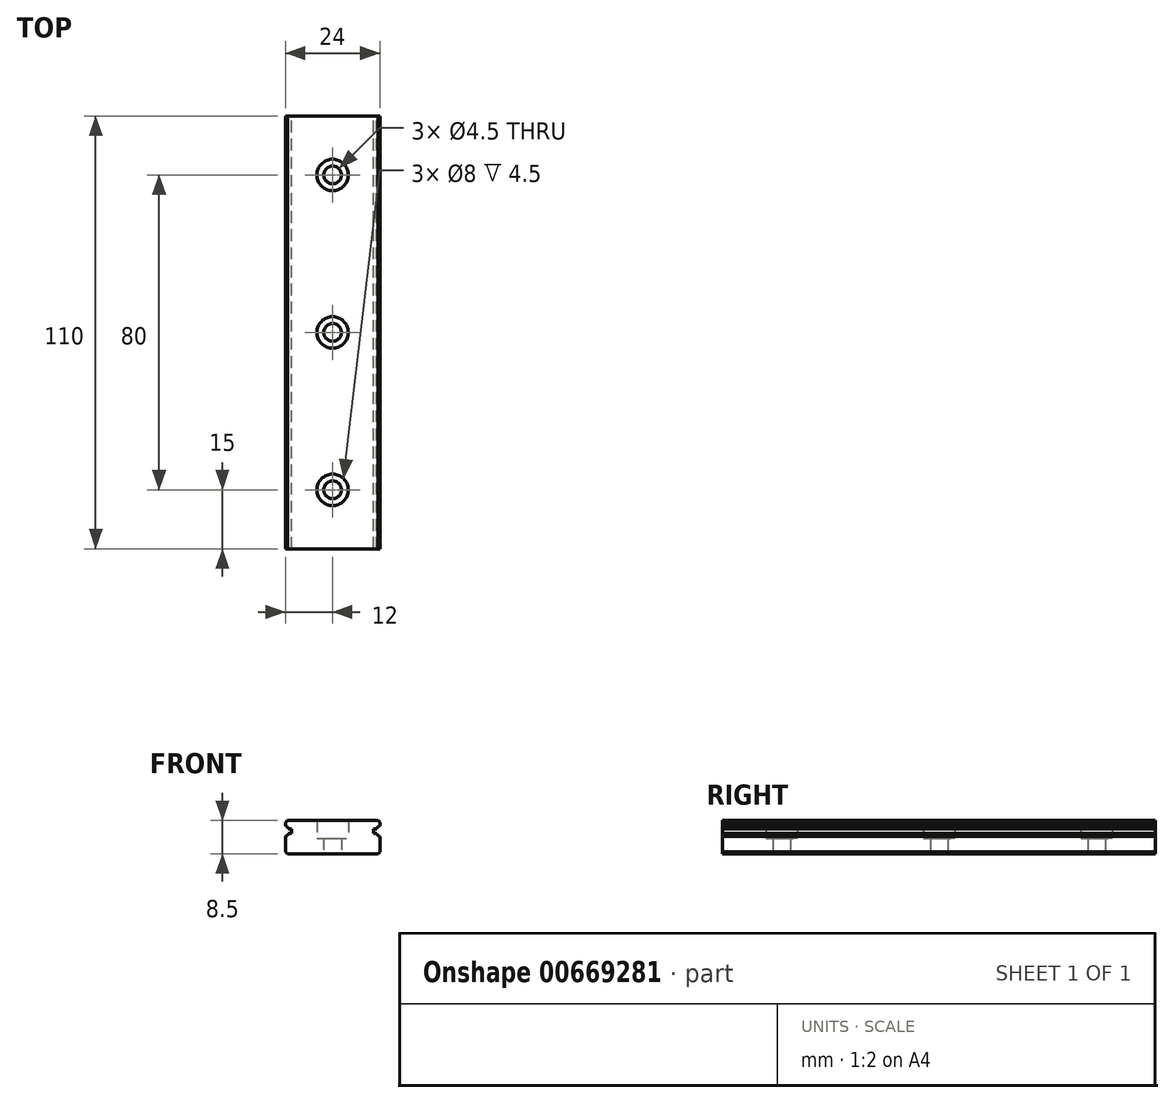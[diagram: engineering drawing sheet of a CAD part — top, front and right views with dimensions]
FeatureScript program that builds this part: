
annotation { "Feature Type Name" : "Feature", "Feature Type Description" : "" }
export const myFeature = defineFeature(function(context is Context, id is Id, definition is map)
    precondition{}
    {
        {
            assignVariable(context, id + "F0", {"variableType" : VariableType.LENGTH, "name" : "D", "lengthValue" : 8 * mm});
        }
        {
            assignVariable(context, id + "F1", {"variableType" : VariableType.LENGTH, "name" : "d", "lengthValue" : 4.5 * mm});
        }
        {
            assignVariable(context, id + "F2", {"variableType" : VariableType.LENGTH, "name" : "h", "lengthValue" : 4.5 * mm});
        }
        {
            var Q0;
            Q0=qCreatedBy(makeId("Front.planeOp"),FACE);
            var sketch = newSketch(context, id + "F3", { "sketchPlane" : qUnion([Q0])});
            skLineSegment(sketch, "E0.bottom", {"start": v(0, -4.25) * mm, "end": v(-11.5, -4.25) * mm});
            skLineSegment(sketch, "E0.right", {"start": v(-12, -3.76) * mm, "end": v(-12, 0.22) * mm});
            skArc(sketch, "E1", {"start": v(-12, 0.22) * mm, "mid": v(-11.5, 0.52) * mm, "end": v(-11.15, 1) * mm});
            skLineSegment(sketch, "E2", {"start": v(-10.45, 1) * mm, "end": v(-11.15, 1) * mm});
            skLineSegment(sketch, "E3", {"start": v(-10.45, 2.1) * mm, "end": v(-11.15, 2.1) * mm});
            skLineSegment(sketch, "E4", {"start": v(-12, 3.76) * mm, "end": v(-11.5, 4.25) * mm});
            skLineSegment(sketch, "E5.MirrorCS", {"start": v(-12, -3.76) * mm, "end": v(-11.5, -4.25) * mm});
            skPoint(sketch, "E6.orphan", {"position": v(-12, 4.25) * mm});
            skLineSegment(sketch, "E7.trimOffspring", {"start": v(-12, 2.88) * mm, "end": v(-12, 3.76) * mm});
            skArc(sketch, "E8.trimOffspring", {"start": v(-11.15, 2.1) * mm, "mid": v(-11.5, 2.58) * mm, "end": v(-12, 2.88) * mm});
            skPoint(sketch, "E9.orphan", {"position": v(-12, -4.25) * mm});
            skLineSegment(sketch, "E10", {"start": v(-11.5, 4.25) * mm, "end": v(0, 4.25) * mm});
            skLineSegment(sketch, "E11", {"start": v(-10.45, 2.1) * mm, "end": v(-10.45, 1) * mm});
            skLineSegment(sketch, "E12", {"start": v(-12.44, 1.55) * mm, "end": v(0, 1.55) * mm, "construction": true});
            skLineSegment(sketch, "E13.MirrorCS", {"start": v(12, 3.76) * mm, "end": v(11.5, 4.25) * mm});
            skLineSegment(sketch, "E14.MirrorCS", {"start": v(12, -3.76) * mm, "end": v(11.5, -4.25) * mm});
            skLineSegment(sketch, "E15.MirrorCS", {"start": v(10.45, 2.1) * mm, "end": v(10.45, 1) * mm});
            skLineSegment(sketch, "E16.MirrorCS", {"start": v(12, 2.88) * mm, "end": v(12, 3.76) * mm});
            skPoint(sketch, "E17.MirrorP", {"position": v(12, 4.25) * mm});
            skPoint(sketch, "E18.MirrorP", {"position": v(12, -4.25) * mm});
            skLineSegment(sketch, "E19.MirrorCS", {"start": v(12, -3.76) * mm, "end": v(12, 0.22) * mm});
            skArc(sketch, "E20.MirrorCS", {"start": v(12, 0.22) * mm, "mid": v(11.5, 0.52) * mm, "end": v(11.15, 1) * mm});
            skLineSegment(sketch, "E21.MirrorCS", {"start": v(10.45, 1) * mm, "end": v(11.15, 1) * mm});
            skLineSegment(sketch, "E22.MirrorCS", {"start": v(10.45, 2.1) * mm, "end": v(11.15, 2.1) * mm});
            skArc(sketch, "E23.MirrorCS", {"start": v(11.15, 2.1) * mm, "mid": v(11.5, 2.58) * mm, "end": v(12, 2.88) * mm});
            skLineSegment(sketch, "E24.MirrorCS", {"start": v(11.5, 4.25) * mm, "end": v(0, 4.25) * mm});
            skLineSegment(sketch, "E25.MirrorCS", {"start": v(0, -4.25) * mm, "end": v(11.5, -4.25) * mm});
            skSolve(sketch);
        }
        {
            var Q0;
            Q0=makeQuery(id+"F3.imprint","IMPRINT",FACE,{"disambiguationData":[TD([[makeQuery(id+"F3.imprint","IMPRINT",EDGE,{"derivedFrom":sQuery(id+"F3.wireOp",EDGE,"E0.bottom")}),-1.0]])]});
            extrude(context, id + "F4", {"entities" : qUnion([Q0]), "depth" : 110 * mm, "offsetDistance" : 25 * mm});
        }
        {
            var Q0;
            Q0=makeQuery(id+"F4.opExtrude","SWEPT_FACE",FACE,{"disambiguationData":[OSD([sQuery(id+"F3.wireOp",EDGE,"E10"),sQuery(id+"F3.wireOp",EDGE,"E24.MirrorCS")])]});
            var sketch = newSketch(context, id + "F5", { "sketchPlane" : qUnion([Q0])});
            skPoint(sketch, "E26", {"position": v(0, -15) * mm});
            skPoint(sketch, "E27.0.1.0", {"position": v(0, -55) * mm});
            skPoint(sketch, "E27.0.2.0", {"position": v(0, -95) * mm});
            skPoint(sketch, "E27.0.3.0", {"position": v(0, -135) * mm});
            skPoint(sketch, "E27.0.4.0", {"position": v(0, -175) * mm});
            skPoint(sketch, "E27.0.5.0", {"position": v(0, -215) * mm});
            skPoint(sketch, "E27.0.6.0", {"position": v(0, -255) * mm});
            skPoint(sketch, "E27.0.7.0", {"position": v(0, -295) * mm});
            skPoint(sketch, "E27.0.8.0", {"position": v(0, -335) * mm});
            skPoint(sketch, "E27.0.9.0", {"position": v(0, -375) * mm});
            skPoint(sketch, "E27.0.10.0", {"position": v(0, -415) * mm});
            skPoint(sketch, "E27.0.11.0", {"position": v(0, -455) * mm});
            skPoint(sketch, "E27.0.12.0", {"position": v(0, -495) * mm});
            skPoint(sketch, "E27.0.13.0", {"position": v(0, -535) * mm});
            skPoint(sketch, "E27.0.14.0", {"position": v(0, -575) * mm});
            skPoint(sketch, "E27.0.15.0", {"position": v(0, -615) * mm});
            skPoint(sketch, "E27.0.16.0", {"position": v(0, -655) * mm});
            skPoint(sketch, "E27.0.17.0", {"position": v(0, -695) * mm});
            skPoint(sketch, "E27.0.18.0", {"position": v(0, -735) * mm});
            skPoint(sketch, "E27.0.19.0", {"position": v(0, -775) * mm});
            skPoint(sketch, "E27.0.20.0", {"position": v(0, -815) * mm});
            skPoint(sketch, "E27.0.21.0", {"position": v(0, -855) * mm});
            skPoint(sketch, "E27.0.22.0", {"position": v(0, -895) * mm});
            skPoint(sketch, "E27.0.23.0", {"position": v(0, -935) * mm});
            skPoint(sketch, "E27.0.24.0", {"position": v(0, -975) * mm});
            skPoint(sketch, "E27.0.25.0", {"position": v(0, -1015) * mm});
            skPoint(sketch, "E27.0.26.0", {"position": v(0, -1055) * mm});
            skPoint(sketch, "E27.0.27.0", {"position": v(0, -1095) * mm});
            skPoint(sketch, "E27.0.28.0", {"position": v(0, -1135) * mm});
            skPoint(sketch, "E27.0.29.0", {"position": v(0, -1175) * mm});
            skPoint(sketch, "E27.0.30.0", {"position": v(0, -1215) * mm});
            skPoint(sketch, "E27.0.31.0", {"position": v(0, -1255) * mm});
            skPoint(sketch, "E27.0.32.0", {"position": v(0, -1295) * mm});
            skPoint(sketch, "E27.0.33.0", {"position": v(0, -1335) * mm});
            skPoint(sketch, "E27.0.34.0", {"position": v(0, -1375) * mm});
            skPoint(sketch, "E27.0.35.0", {"position": v(0, -1415) * mm});
            skPoint(sketch, "E27.0.36.0", {"position": v(0, -1455) * mm});
            skPoint(sketch, "E27.0.37.0", {"position": v(0, -1495) * mm});
            skPoint(sketch, "E27.0.38.0", {"position": v(0, -1535) * mm});
            skPoint(sketch, "E27.0.39.0", {"position": v(0, -1575) * mm});
            skPoint(sketch, "E27.0.40.0", {"position": v(0, -1615) * mm});
            skPoint(sketch, "E27.0.41.0", {"position": v(0, -1655) * mm});
            skPoint(sketch, "E27.0.42.0", {"position": v(0, -1695) * mm});
            skPoint(sketch, "E27.0.43.0", {"position": v(0, -1735) * mm});
            skPoint(sketch, "E27.0.44.0", {"position": v(0, -1775) * mm});
            skPoint(sketch, "E27.0.45.0", {"position": v(0, -1815) * mm});
            skPoint(sketch, "E27.0.46.0", {"position": v(0, -1855) * mm});
            skPoint(sketch, "E27.0.47.0", {"position": v(0, -1895) * mm});
            skPoint(sketch, "E27.0.48.0", {"position": v(0, -1935) * mm});
            skPoint(sketch, "E27.0.49.0", {"position": v(0, -1975) * mm});
            skLineSegment(sketch, "E27.direction1", {"start": v(0, -15) * mm, "end": v(25, -15) * mm, "construction": true});
            skLineSegment(sketch, "E27.direction2", {"start": v(0, -15) * mm, "end": v(0, -55) * mm, "construction": true});
            skSolve(sketch);
        }
        {
            var Q0;
            Q0=sQuery(id+"F5.wireOp",VERTEX,"E27.0.2.0");
            var Q1;
            Q1=sQuery(id+"F5.wireOp",VERTEX,"E27.0.8.0");
            var Q2;
            Q2=sQuery(id+"F5.wireOp",VERTEX,"E26");
            var Q3;
            Q3=sQuery(id+"F5.wireOp",VERTEX,"E27.0.11.0");
            var Q4;
            Q4=sQuery(id+"F5.wireOp",VERTEX,"E27.0.7.0");
            var Q5;
            Q5=sQuery(id+"F5.wireOp",VERTEX,"E27.0.12.0");
            var Q6;
            Q6=sQuery(id+"F5.wireOp",VERTEX,"E27.0.4.0");
            var Q7;
            Q7=sQuery(id+"F5.wireOp",VERTEX,"E27.0.3.0");
            var Q8;
            Q8=sQuery(id+"F5.wireOp",VERTEX,"E27.0.6.0");
            var Q9;
            Q9=sQuery(id+"F5.wireOp",VERTEX,"E27.0.10.0");
            var Q10;
            Q10=sQuery(id+"F5.wireOp",VERTEX,"E27.0.5.0");
            var Q11;
            Q11=sQuery(id+"F5.wireOp",VERTEX,"E27.0.15.0");
            var Q12;
            Q12=sQuery(id+"F5.wireOp",VERTEX,"E27.0.9.0");
            var Q13;
            Q13=sQuery(id+"F5.wireOp",VERTEX,"E27.0.14.0");
            var Q14;
            Q14=sQuery(id+"F5.wireOp",VERTEX,"E27.0.13.0");
            var Q15;
            Q15=sQuery(id+"F5.wireOp",VERTEX,"E27.0.1.0");
            var Q16;
            Q16=sQuery(id+"F5.wireOp",VERTEX,"E27.0.38.0");
            var Q17;
            Q17=sQuery(id+"F5.wireOp",VERTEX,"E27.0.26.0");
            var Q18;
            Q18=sQuery(id+"F5.wireOp",VERTEX,"E27.0.34.0");
            var Q19;
            Q19=sQuery(id+"F5.wireOp",VERTEX,"E27.0.40.0");
            var Q20;
            Q20=sQuery(id+"F5.wireOp",VERTEX,"E27.0.30.0");
            var Q21;
            Q21=sQuery(id+"F5.wireOp",VERTEX,"E27.0.19.0");
            var Q22;
            Q22=sQuery(id+"F5.wireOp",VERTEX,"E27.0.29.0");
            var Q23;
            Q23=sQuery(id+"F5.wireOp",VERTEX,"E27.0.36.0");
            var Q24;
            Q24=sQuery(id+"F5.wireOp",VERTEX,"E27.0.33.0");
            var Q25;
            Q25=sQuery(id+"F5.wireOp",VERTEX,"E27.0.37.0");
            var Q26;
            Q26=sQuery(id+"F5.wireOp",VERTEX,"E27.0.32.0");
            var Q27;
            Q27=sQuery(id+"F5.wireOp",VERTEX,"E27.0.31.0");
            var Q28;
            Q28=sQuery(id+"F5.wireOp",VERTEX,"E27.0.24.0");
            var Q29;
            Q29=sQuery(id+"F5.wireOp",VERTEX,"E27.0.25.0");
            var Q30;
            Q30=sQuery(id+"F5.wireOp",VERTEX,"E27.0.20.0");
            var Q31;
            Q31=sQuery(id+"F5.wireOp",VERTEX,"E27.0.23.0");
            var Q32;
            Q32=sQuery(id+"F5.wireOp",VERTEX,"E27.0.17.0");
            var Q33;
            Q33=sQuery(id+"F5.wireOp",VERTEX,"E27.0.21.0");
            var Q34;
            Q34=sQuery(id+"F5.wireOp",VERTEX,"E27.0.28.0");
            var Q35;
            Q35=sQuery(id+"F5.wireOp",VERTEX,"E27.0.22.0");
            var Q36;
            Q36=sQuery(id+"F5.wireOp",VERTEX,"E27.0.18.0");
            var Q37;
            Q37=sQuery(id+"F5.wireOp",VERTEX,"E27.0.39.0");
            var Q38;
            Q38=sQuery(id+"F5.wireOp",VERTEX,"E27.0.27.0");
            var Q39;
            Q39=sQuery(id+"F5.wireOp",VERTEX,"E27.0.35.0");
            var Q40;
            Q40=sQuery(id+"F5.wireOp",VERTEX,"E27.0.41.0");
            var Q41;
            Q41=sQuery(id+"F5.wireOp",VERTEX,"E27.0.16.0");
            var Q42;
            Q42=sQuery(id+"F5.wireOp",VERTEX,"E27.0.47.0");
            var Q43;
            Q43=sQuery(id+"F5.wireOp",VERTEX,"E27.0.44.0");
            var Q44;
            Q44=sQuery(id+"F5.wireOp",VERTEX,"E27.0.42.0");
            var Q45;
            Q45=sQuery(id+"F5.wireOp",VERTEX,"E27.0.49.0");
            var Q46;
            Q46=sQuery(id+"F5.wireOp",VERTEX,"E27.0.45.0");
            var Q47;
            Q47=sQuery(id+"F5.wireOp",VERTEX,"E27.0.48.0");
            var Q48;
            Q48=sQuery(id+"F5.wireOp",VERTEX,"E27.0.43.0");
            var Q49;
            Q49=sQuery(id+"F5.wireOp",VERTEX,"E27.0.46.0");
            var Q50;
            Q50=makeQuery(id+"F4.opExtrude","SWEPT_BODY",BODY,{"disambiguationData":[OSD([sQuery(id+"F3.wireOp",EDGE,"E0.bottom"),sQuery(id+"F3.wireOp",EDGE,"E0.right"),sQuery(id+"F3.wireOp",EDGE,"E1"),sQuery(id+"F3.wireOp",EDGE,"E2"),sQuery(id+"F3.wireOp",EDGE,"E3"),sQuery(id+"F3.wireOp",EDGE,"E4"),sQuery(id+"F3.wireOp",EDGE,"E5.MirrorCS"),sQuery(id+"F3.wireOp",EDGE,"E7.trimOffspring"),sQuery(id+"F3.wireOp",EDGE,"E8.trimOffspring"),sQuery(id+"F3.wireOp",EDGE,"E10"),sQuery(id+"F3.wireOp",EDGE,"E11"),sQuery(id+"F3.wireOp",EDGE,"E13.MirrorCS"),sQuery(id+"F3.wireOp",EDGE,"E14.MirrorCS"),sQuery(id+"F3.wireOp",EDGE,"E15.MirrorCS"),sQuery(id+"F3.wireOp",EDGE,"E16.MirrorCS"),sQuery(id+"F3.wireOp",EDGE,"E19.MirrorCS"),sQuery(id+"F3.wireOp",EDGE,"E20.MirrorCS"),sQuery(id+"F3.wireOp",EDGE,"E21.MirrorCS"),sQuery(id+"F3.wireOp",EDGE,"E22.MirrorCS"),sQuery(id+"F3.wireOp",EDGE,"E23.MirrorCS"),sQuery(id+"F3.wireOp",EDGE,"E24.MirrorCS"),sQuery(id+"F3.wireOp",EDGE,"E25.MirrorCS")])]});
            hole(context, id + "F6", {"style" : HoleStyle.C_BORE, "endStyle" : HoleEndStyle.THROUGH, "holeDiameter" : getVariable(context, 'd'), "cBoreDiameter" : getVariable(context, 'D'), "cBoreDepth" : getVariable(context, 'h'), "majorDiameter" : 5 * mm, "isTappedThrough" : true, "tappedDepth" : 1 * mm, "tapClearance" : 3, "locations" : qUnion([Q0, Q1, Q2, Q3, Q4, Q5, Q6, Q7, Q8, Q9, Q10, Q11, Q12, Q13, Q14, Q15, Q16, Q17, Q18, Q19, Q20, Q21, Q22, Q23, Q24, Q25, Q26, Q27, Q28, Q29, Q30, Q31, Q32, Q33, Q34, Q35, Q36, Q37, Q38, Q39, Q40, Q41, Q42, Q43, Q44, Q45, Q46, Q47, Q48, Q49]), "scope" : qUnion([Q50]), "startStyle" : HoleStartStyle.PART});
        }
    });
